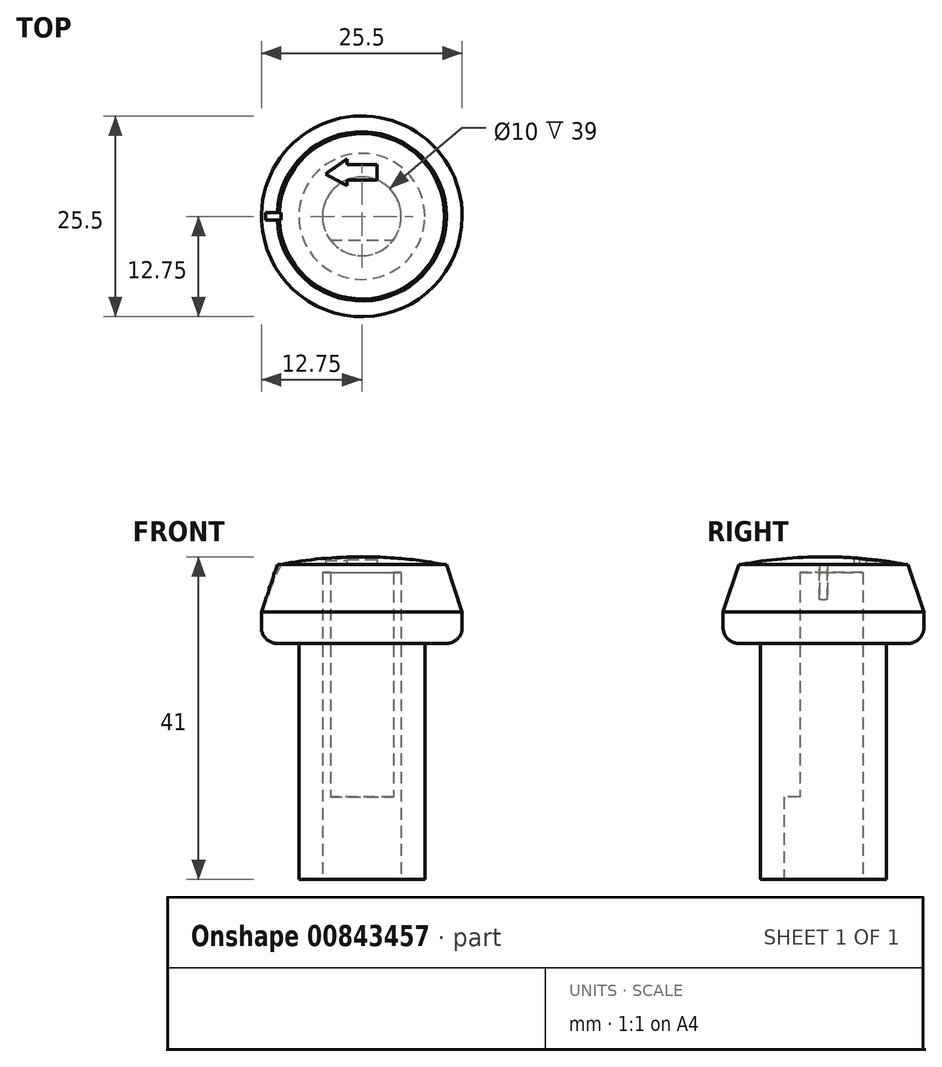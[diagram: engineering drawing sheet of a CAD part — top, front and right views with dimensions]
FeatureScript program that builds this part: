
annotation { "Feature Type Name" : "Feature", "Feature Type Description" : "" }
export const myFeature = defineFeature(function(context is Context, id is Id, definition is map)
    precondition{}
    {
        {
            var Q0;
            Q0=qCreatedBy(makeId("Top.planeOp"),FACE);
            var sketch = newSketch(context, id + "F0", { "sketchPlane" : qUnion([Q0])});
            skCircle(sketch, "E0", {"center": v(0, 0) * mm, "radius": 8 * mm});
            skSolve(sketch);
        }
        {
            var Q0;
            Q0=makeQuery(id+"F0.imprint","IMPRINT",FACE,{"disambiguationData":[TD([[makeQuery(id+"F0.imprint","IMPRINT",EDGE,{"derivedFrom":sQuery(id+"F0.wireOp",EDGE,"E0")}),1.0]])]});
            var Q1;
            Q1=sQuery(id+"F0.wireOp",EDGE,"E0");
            extrude(context, id + "F1", {"entities" : qUnion([Q0]), "surfaceEntities" : qUnion([Q1]), "oppositeDirection" : true, "depth" : 30 * mm, "offsetDistance" : 25 * mm});
        }
        {
            var Q0;
            Q0=qCreatedBy(makeId("Top.planeOp"),FACE);
            var sketch = newSketch(context, id + "F2", { "sketchPlane" : qUnion([Q0])});
            skCircle(sketch, "E1", {"center": v(0, 0) * mm, "radius": 12.75 * mm});
            skSolve(sketch);
        }
        {
            var Q0;
            Q0=makeQuery(id+"F2.imprint","IMPRINT",FACE,{"disambiguationData":[TD([[makeQuery(id+"F2.imprint","IMPRINT",EDGE,{"derivedFrom":sQuery(id+"F2.wireOp",EDGE,"E1")}),1.0]])]});
            extrude(context, id + "F3", {"entities" : qUnion([Q0]), "depth" : 10 * mm, "offsetDistance" : 25 * mm});
        }
        {
            var Q0;
            Q0=makeQuery(id+"F3.opExtrude","CAP_EDGE",EDGE,{"disambiguationData":[OSD([sQuery(id+"F2.wireOp",EDGE,"E1")])],"isStart":false});
            chamfer(context, id + "F4", {"entities" : qUnion([Q0]), "chamferType" : ChamferType.TWO_OFFSETS, "width1" : 2 * mm, "oppositeDirection" : false, "width2" : 6 * mm, "tangentPropagation" : true});
        }
        {
            var Q0;
            Q0=qCreatedBy(makeId("Front.planeOp"),FACE);
            var sketch = newSketch(context, id + "F5", { "sketchPlane" : qUnion([Q0])});
            skArc(sketch, "E2", {"start": v(10.5, 10) * mm, "mid": v(5.27, 10.75) * mm, "end": v(0, 11) * mm});
            skLineSegment(sketch, "E3", {"start": v(10.5, 10) * mm, "end": v(0, 10) * mm});
            skLineSegment(sketch, "E4", {"start": v(0, 14.36) * mm, "end": v(0, 8.46) * mm, "construction": true});
            skLineSegment(sketch, "E5", {"start": v(0, 11) * mm, "end": v(0, 10) * mm});
            skSolve(sketch);
        }
        {
            var Q0;
            Q0=makeQuery(id+"F5.imprint","IMPRINT",FACE,{"disambiguationData":[TD([[makeQuery(id+"F5.imprint","IMPRINT",EDGE,{"derivedFrom":sQuery(id+"F5.wireOp",EDGE,"E2")}),1.0]])]});
            var Q1;
            Q1=sQuery(id+"F5.wireOp",EDGE,"E4");
            revolve(context, id + "F6", {"operationType" : NewBodyOperationType.ADD, "surfaceOperationType" : NewSurfaceOperationType.NEW, "entities" : qUnion([Q0]), "axis" : qUnion([Q1]), "revolveType" : RevolveType.FULL});
        }
        {
            var Q0;
            Q0=makeQuery(id+"F3.opExtrude","CAP_EDGE",EDGE,{"disambiguationData":[OSD([sQuery(id+"F2.wireOp",EDGE,"E1")])],"isStart":true});
            fillet(context, id + "F7", {"entities" : qUnion([Q0]), "radius" : 2 * mm, "tangentPropagation" : true, "allowEdgeOverflow" : false});
        }
        {
            var Q0;
            Q0=makeQuery(id+"F1.opExtrude","CAP_FACE",FACE,{"disambiguationData":[OSD([sQuery(id+"F0.wireOp",EDGE,"E0")])],"isStart":false});
            var sketch = newSketch(context, id + "F8", { "sketchPlane" : qUnion([Q0])});
            skCircle(sketch, "E6", {"center": v(0, 0) * mm, "radius": 5 * mm});
            skSolve(sketch);
        }
        {
            var Q0;
            Q0=makeQuery(id+"F8.imprint","IMPRINT",FACE,{"disambiguationData":[TD([[makeQuery(id+"F8.imprint","IMPRINT",EDGE,{"derivedFrom":sQuery(id+"F8.wireOp",EDGE,"E6")}),1.0]])]});
            extrude(context, id + "F9", {"entities" : qUnion([Q0]), "operationType" : NewBodyOperationType.REMOVE, "oppositeDirection" : true, "depth" : 39 * mm, "offsetDistance" : 25 * mm});
        }
        {
            var Q0;
            Q0=makeQuery(id+"F9.boolean.opBoolean","COPY",FACE,{"derivedFrom":makeQuery(id+"F9.opExtrude","CAP_FACE",FACE,{"disambiguationData":[OSD([sQuery(id+"F8.wireOp",EDGE,"E6")])],"isStart":false})});
            var sketch = newSketch(context, id + "F10", { "sketchPlane" : qUnion([Q0])});
            skLineSegment(sketch, "E7", {"start": v(-4.87, 3) * mm, "end": v(5.04, 3) * mm});
            skLineSegment(sketch, "E8", {"start": v(5.04, 3) * mm, "end": v(0, 6) * mm});
            skLineSegment(sketch, "E9", {"start": v(0, 6) * mm, "end": v(-4.87, 3) * mm});
            skSolve(sketch);
        }
        {
            var Q0;
            Q0 = qSketchRegion(id + "F10", true);
            extrude(context, id + "F11", {"entities" : qUnion([Q0]), "operationType" : NewBodyOperationType.ADD, "depth" : 28.5 * mm, "offsetDistance" : 25 * mm});
        }
        {
            var Q0;
            Q0=qCreatedBy(makeId("Front.planeOp"),FACE);
            var sketch = newSketch(context, id + "F12", { "sketchPlane" : qUnion([Q0])});
            skLineSegment(sketch, "E10", {"start": v(-9.99, 10.72) * mm, "end": v(-13.34, 2.99) * mm});
            skLineSegment(sketch, "E11", {"start": v(-13.34, 2.99) * mm, "end": v(-16.76, 4.47) * mm});
            skLineSegment(sketch, "E12", {"start": v(-16.76, 4.47) * mm, "end": v(-13.1, 12.89) * mm});
            skLineSegment(sketch, "E13", {"start": v(-13.1, 12.89) * mm, "end": v(-9.99, 10.72) * mm});
            skSolve(sketch);
        }
        {
            var Q0;
            Q0 = qSketchRegion(id + "F12", true);
            extrude(context, id + "F13", {"entities" : qUnion([Q0]), "operationType" : NewBodyOperationType.REMOVE, "endBound" : BoundingType.SYMMETRIC, "oppositeDirection" : true, "depth" : 1 * mm, "offsetDistance" : 25 * mm});
        }
        {
            var Q0;
            {var subQ0=sQuery(id+"F2.wireOp",EDGE,"E1");var subQ3=sQuery(id+"F12.wireOp",EDGE,"E13");var subQ4=sQuery(id+"F12.wireOp",EDGE,"E12");var subQ5=sQuery(id+"F12.wireOp",EDGE,"E11");var subQ6=sQuery(id+"F12.wireOp",EDGE,"E10");var subQ7=makeQuery(id+"FZQSXFymNiOWYtq_2.9.F13.opExtrude","CAP_FACE",FACE,{"disambiguationData":[OSD([subQ6,subQ5,subQ4,subQ3])],"isStart":true});var subQ8=makeQuery(id+"F13.boolean.opBoolean","COPY",FACE,{"derivedFrom":makeQuery(id+"F13.opExtrude","CAP_FACE",FACE,{"disambiguationData":[OSD([subQ6,subQ5,subQ4,subQ3])],"isStart":false})});Q0=makeQuery(id+"FZQSXFymNiOWYtq_2.10.F13.boolean.opBoolean","SPLIT",FACE,{"disambiguationData":[TD([makeQuery(id+"FZQSXFymNiOWYtq_2.9.F13.boolean.opBoolean","COPY",FACE,{"derivedFrom":subQ7})])],"derivedFrom":makeQuery(id+"FZQSXFymNiOWYtq_2.9.F13.boolean.opBoolean","SPLIT",FACE,{"disambiguationData":[TD([subQ8])],"derivedFrom":makeQuery(id+"FZQSXFymNiOWYtq_2.8.F13.boolean.opBoolean","SPLIT",FACE,{"disambiguationData":[TD([subQ8])],"derivedFrom":makeQuery(id+"FZQSXFymNiOWYtq_2.7.F13.boolean.opBoolean","SPLIT",FACE,{"disambiguationData":[TD([subQ8])],"derivedFrom":makeQuery(id+"FZQSXFymNiOWYtq_2.6.F13.boolean.opBoolean","SPLIT",FACE,{"disambiguationData":[TD([subQ8])],"derivedFrom":makeQuery(id+"FZQSXFymNiOWYtq_2.5.F13.boolean.opBoolean","SPLIT",FACE,{"disambiguationData":[TD([subQ8])],"derivedFrom":makeQuery(id+"FZQSXFymNiOWYtq_2.4.F13.boolean.opBoolean","SPLIT",FACE,{"disambiguationData":[TD([subQ8])],"derivedFrom":makeQuery(id+"FZQSXFymNiOWYtq_2.3.F13.boolean.opBoolean","SPLIT",FACE,{"disambiguationData":[TD([subQ8])],"derivedFrom":makeQuery(id+"FZQSXFymNiOWYtq_2.2.F13.boolean.opBoolean","SPLIT",FACE,{"disambiguationData":[TD([subQ8])],"derivedFrom":makeQuery(id+"FZQSXFymNiOWYtq_2.1.F13.boolean.opBoolean","SPLIT",FACE,{"disambiguationData":[TD([subQ8])],"derivedFrom":makeQuery(id+"F3.opExtrude","CAP_FACE",FACE,{"disambiguationData":[OSD([subQ0])],"isStart":false})})})})})})})})})})});}
            var sketch = newSketch(context, id + "F14", { "sketchPlane" : qUnion([Q0])});
            skLineSegment(sketch, "E14", {"start": v(1.93, 6.58) * mm, "end": v(1.93, 4.58) * mm});
            skLineSegment(sketch, "E15", {"start": v(1.93, 4.58) * mm, "end": v(-1.9, 4.58) * mm});
            skLineSegment(sketch, "E16", {"start": v(-1.9, 4.58) * mm, "end": v(-1.9, 3.88) * mm});
            skLineSegment(sketch, "E17", {"start": v(-1.9, 3.88) * mm, "end": v(-4.62, 5.38) * mm});
            skLineSegment(sketch, "E18", {"start": v(-4.62, 5.38) * mm, "end": v(-1.9, 7.28) * mm});
            skLineSegment(sketch, "E19", {"start": v(-1.9, 7.28) * mm, "end": v(-1.9, 6.58) * mm});
            skLineSegment(sketch, "E20", {"start": v(-1.9, 6.58) * mm, "end": v(1.93, 6.58) * mm});
            skSolve(sketch);
        }
        {
            var Q0;
            Q0 = qSketchRegion(id + "F14", true);
            extrude(context, id + "F15", {"entities" : qUnion([Q0]), "operationType" : NewBodyOperationType.REMOVE, "depth" : 1 * mm, "offsetDistance" : 25 * mm});
        }
    });
